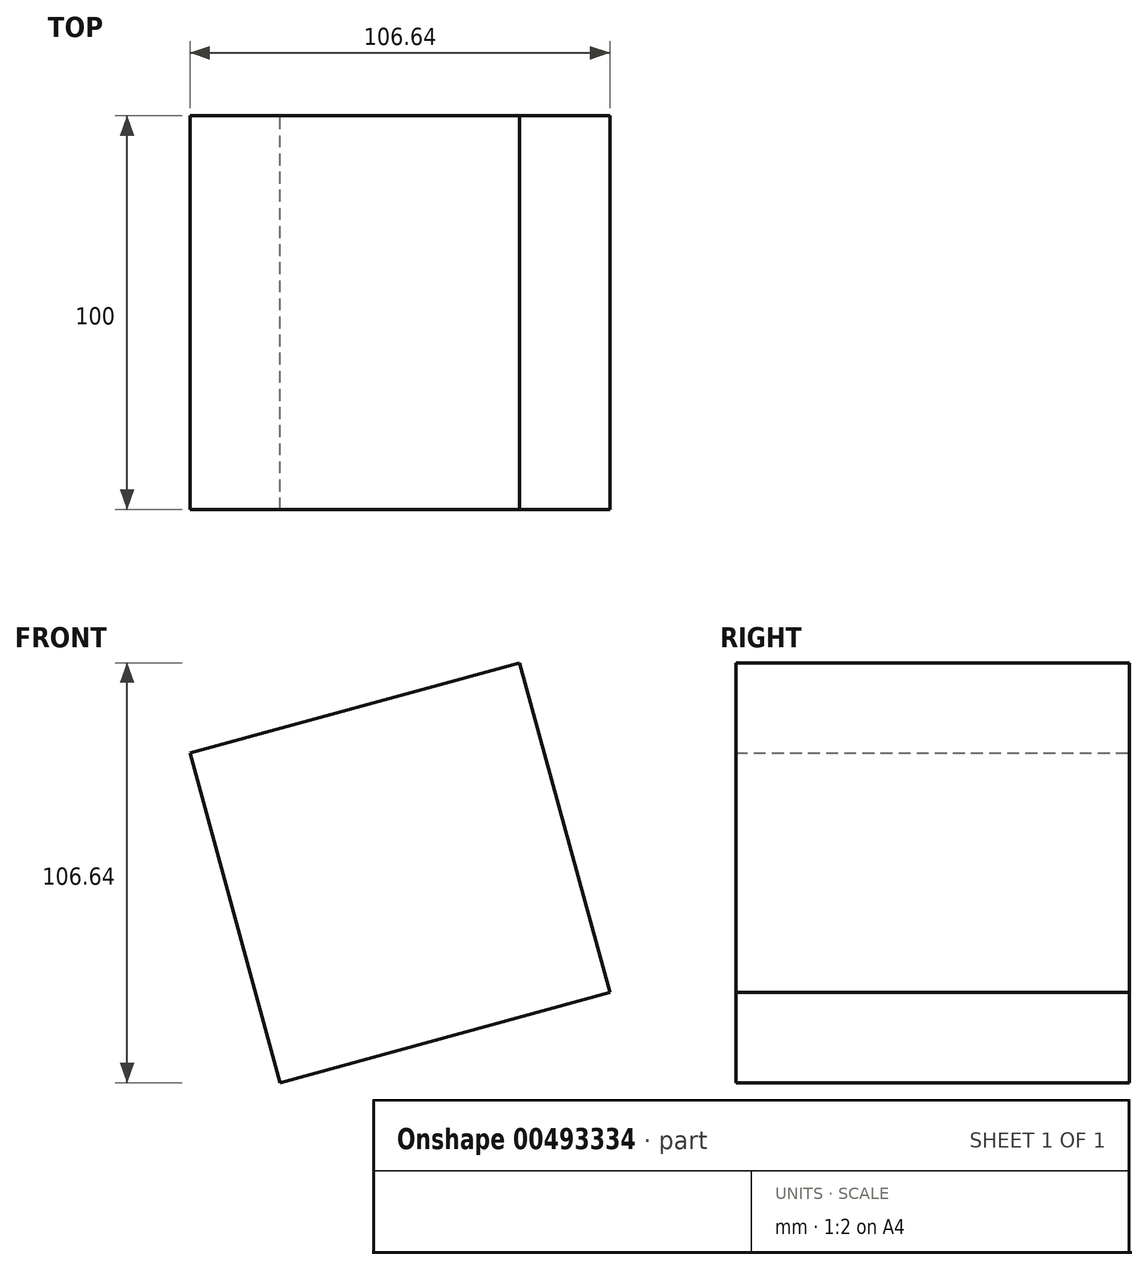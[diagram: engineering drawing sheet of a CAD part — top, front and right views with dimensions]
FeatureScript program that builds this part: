
annotation { "Feature Type Name" : "Feature", "Feature Type Description" : "" }
export const myFeature = defineFeature(function(context is Context, id is Id, definition is map)
    precondition{}
    {
        {
            var Q0;
            Q0=qCreatedBy(makeId("Front.planeOp"),FACE);
            var sketch = newSketch(context, id + "F0", { "sketchPlane" : qUnion([Q0])});
            skCircle(sketch, "E0.cCircle", {"center": v(0, 0) * mm, "radius": 61.38 * mm, "construction": true});
            skLineSegment(sketch, "E0.0", {"start": v(-53.32, 30.39) * mm, "end": v(30.39, 53.32) * mm});
            skLineSegment(sketch, "E0.1", {"start": v(30.39, 53.32) * mm, "end": v(53.32, -30.39) * mm});
            skLineSegment(sketch, "E0.2", {"start": v(53.32, -30.39) * mm, "end": v(-30.39, -53.32) * mm});
            skLineSegment(sketch, "E0.3", {"start": v(-30.39, -53.32) * mm, "end": v(-53.32, 30.39) * mm});
            skSolve(sketch);
        }
        {
            var Q0;
            Q0=makeQuery(id+"F0.imprint","IMPRINT",FACE,{"disambiguationData":[TD([[makeQuery(id+"F0.imprint","IMPRINT",EDGE,{"derivedFrom":sQuery(id+"F0.wireOp",EDGE,"E0.0")}),-1.0]])]});
            extrude(context, id + "F1", {"entities" : qUnion([Q0]), "depth" : 100 * mm});
        }
    });
